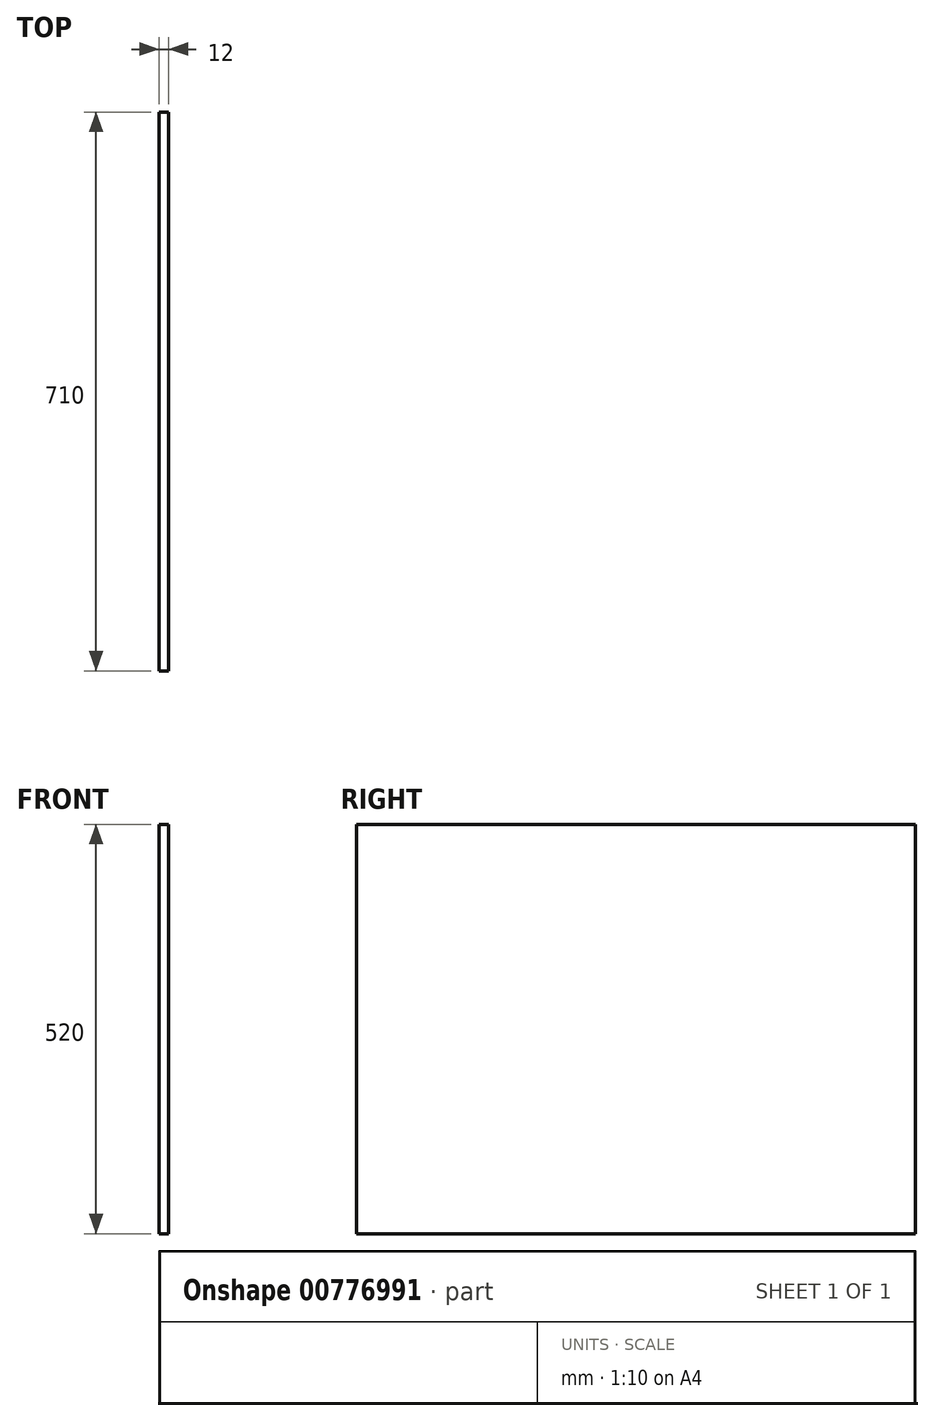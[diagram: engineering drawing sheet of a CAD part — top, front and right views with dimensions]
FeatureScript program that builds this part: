
annotation { "Feature Type Name" : "Feature", "Feature Type Description" : "" }
export const myFeature = defineFeature(function(context is Context, id is Id, definition is map)
    precondition{}
    {
        {
            var Q0;
            Q0=qCreatedBy(makeId("Right.planeOp"),FACE);
            var sketch = newSketch(context, id + "F0", { "sketchPlane" : qUnion([Q0])});
            skLineSegment(sketch, "E0.bottom", {"start": v(-880.72, 520) * mm, "end": v(-170.72, 520) * mm});
            skLineSegment(sketch, "E0.top", {"start": v(-880.72, 0) * mm, "end": v(-170.72, 0) * mm});
            skLineSegment(sketch, "E0.left", {"start": v(-880.72, 520) * mm, "end": v(-880.72, 0) * mm});
            skLineSegment(sketch, "E0.right", {"start": v(-170.72, 520) * mm, "end": v(-170.72, 0) * mm});
            skSolve(sketch);
        }
        {
            var Q0;
            Q0 = qSketchRegion(id + "F0", true);
            extrude(context, id + "F1", {"entities" : qUnion([Q0]), "depth" : 12 * mm, "offsetDistance" : 25 * mm});
        }
    });
